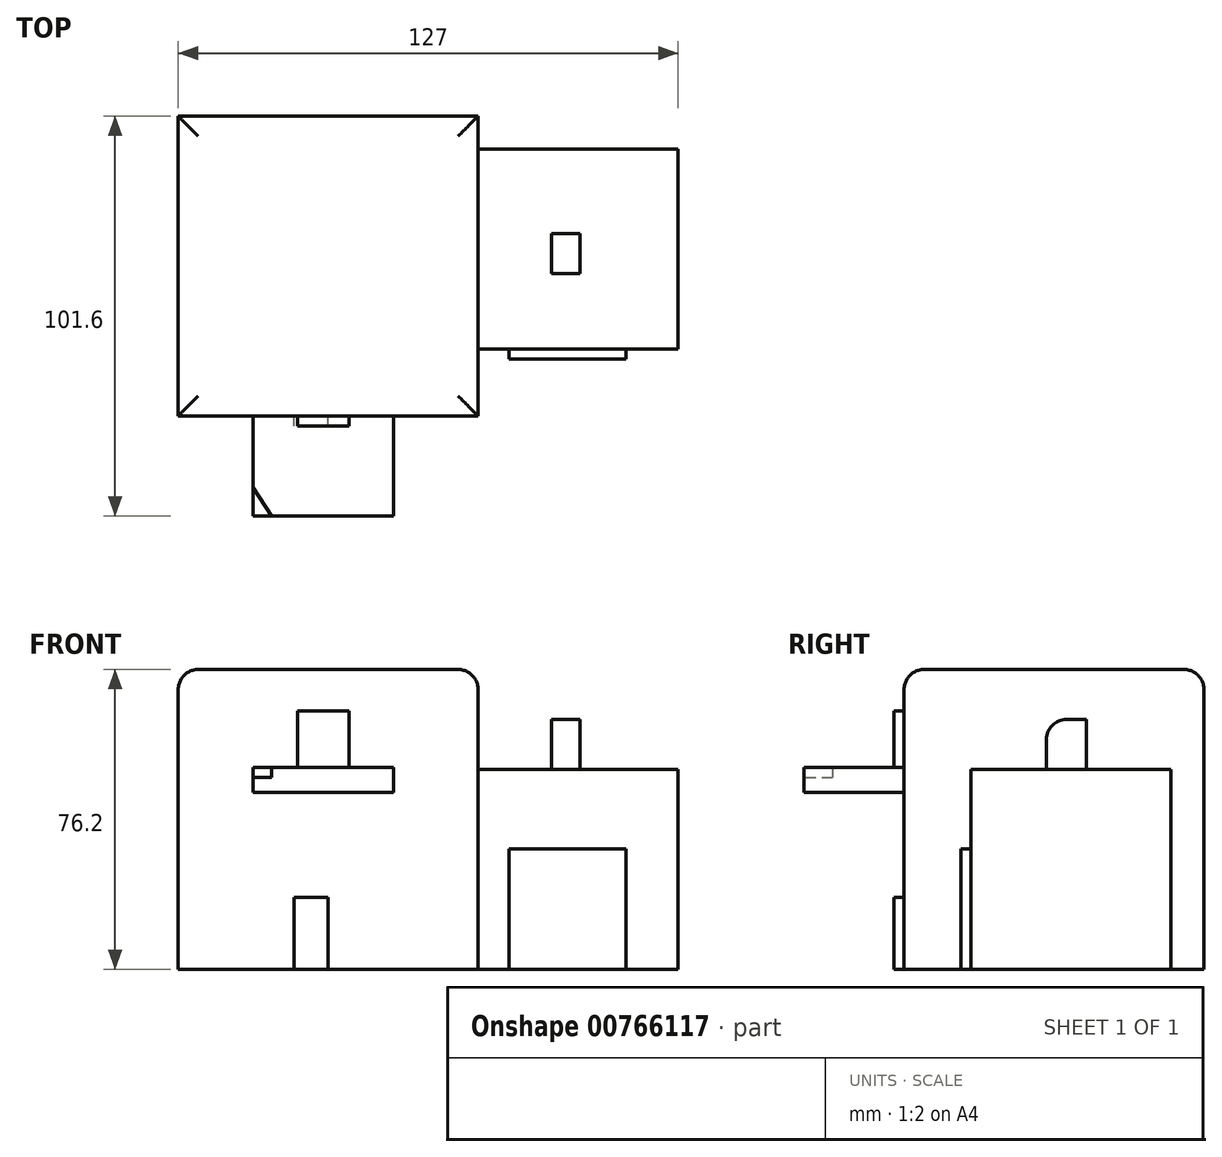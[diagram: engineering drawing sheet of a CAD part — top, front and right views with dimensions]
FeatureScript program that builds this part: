
annotation { "Feature Type Name" : "Feature", "Feature Type Description" : "" }
export const myFeature = defineFeature(function(context is Context, id is Id, definition is map)
    precondition{}
    {
        {
            var Q0;
            Q0=qCreatedBy(makeId("Top.planeOp"),FACE);
            var sketch = newSketch(context, id + "F0", { "sketchPlane" : qUnion([Q0])});
            skLineSegment(sketch, "E0.bottom", {"start": v(0, 0) * mm, "end": v(-76.2, 0) * mm});
            skLineSegment(sketch, "E0.top", {"start": v(0, 76.2) * mm, "end": v(-76.2, 76.2) * mm});
            skLineSegment(sketch, "E0.left", {"start": v(0, 0) * mm, "end": v(0, 76.2) * mm});
            skLineSegment(sketch, "E0.right", {"start": v(-76.2, 0) * mm, "end": v(-76.2, 76.2) * mm});
            skSolve(sketch);
        }
        {
            var Q0;
            Q0=makeQuery(id+"F0.imprint","IMPRINT",FACE,{"disambiguationData":[TD([[makeQuery(id+"F0.imprint","IMPRINT",EDGE,{"derivedFrom":sQuery(id+"F0.wireOp",EDGE,"E0.bottom")}),-1.0]])]});
            extrude(context, id + "F1", {"entities" : qUnion([Q0]), "depth" : 76.2 * mm, "offsetDistance" : 25.4 * mm});
        }
        {
            var Q0;
            Q0=makeQuery(id+"F1.opExtrude","SWEPT_FACE",FACE,{"disambiguationData":[OSD([sQuery(id+"F0.wireOp",EDGE,"E0.left")])]});
            var sketch = newSketch(context, id + "F2", { "sketchPlane" : qUnion([Q0])});
            skLineSegment(sketch, "E1.bottom", {"start": v(17, 0) * mm, "end": v(67.8, 0) * mm});
            skLineSegment(sketch, "E1.top", {"start": v(17, 50.8) * mm, "end": v(67.8, 50.8) * mm});
            skLineSegment(sketch, "E1.left", {"start": v(17, 0) * mm, "end": v(17, 50.8) * mm});
            skLineSegment(sketch, "E1.right", {"start": v(67.8, 0) * mm, "end": v(67.8, 50.8) * mm});
            skSolve(sketch);
        }
        {
            var Q0;
            Q0=makeQuery(id+"F2.imprint","IMPRINT",FACE,{"disambiguationData":[TD([[makeQuery(id+"F2.imprint","IMPRINT",EDGE,{"derivedFrom":sQuery(id+"F2.wireOp",EDGE,"E1.bottom")}),1.0]])]});
            extrude(context, id + "F3", {"entities" : qUnion([Q0]), "operationType" : NewBodyOperationType.ADD, "depth" : 50.8 * mm, "offsetDistance" : 25.4 * mm});
        }
        {
            var Q0;
            Q0=makeQuery(id+"F3.opExtrude","SWEPT_FACE",FACE,{"disambiguationData":[OSD([sQuery(id+"F2.wireOp",EDGE,"E1.top")])]});
            var sketch = newSketch(context, id + "F4", { "sketchPlane" : qUnion([Q0])});
            skLineSegment(sketch, "E2.bottom", {"start": v(25.93, 36.2) * mm, "end": v(18.68, 36.2) * mm});
            skLineSegment(sketch, "E2.top", {"start": v(25.93, 46.31) * mm, "end": v(18.68, 46.31) * mm});
            skLineSegment(sketch, "E2.left", {"start": v(25.93, 36.2) * mm, "end": v(25.93, 46.31) * mm});
            skLineSegment(sketch, "E2.right", {"start": v(18.68, 36.2) * mm, "end": v(18.68, 46.31) * mm});
            skSolve(sketch);
        }
        {
            var Q0;
            Q0=makeQuery(id+"F4.imprint","IMPRINT",FACE,{"disambiguationData":[TD([[makeQuery(id+"F4.imprint","IMPRINT",EDGE,{"derivedFrom":sQuery(id+"F4.wireOp",EDGE,"E2.bottom")}),-1.0]])]});
            extrude(context, id + "F5", {"entities" : qUnion([Q0]), "operationType" : NewBodyOperationType.ADD, "depth" : 12.7 * mm, "offsetDistance" : 25.4 * mm});
        }
        {
            var Q0;
            Q0=makeQuery(id+"F5.opExtrude","CAP_EDGE",EDGE,{"disambiguationData":[OSD([sQuery(id+"F4.wireOp",EDGE,"E2.bottom")])],"isStart":false});
            fillet(context, id + "F6", {"entities" : qUnion([Q0]), "radius" : 5.08 * mm, "tangentPropagation" : true, "allowEdgeOverflow" : false});
        }
        {
            var Q0;
            Q0=makeQuery(id+"F1.opExtrude","SWEPT_FACE",FACE,{"disambiguationData":[OSD([sQuery(id+"F0.wireOp",EDGE,"E0.bottom")])]});
            var sketch = newSketch(context, id + "F7", { "sketchPlane" : qUnion([Q0])});
            skLineSegment(sketch, "E3.bottom", {"start": v(-46.73, 0) * mm, "end": v(-38.14, 0) * mm});
            skLineSegment(sketch, "E3.top", {"start": v(-46.73, 18.26) * mm, "end": v(-38.14, 18.26) * mm});
            skLineSegment(sketch, "E3.left", {"start": v(-46.73, 0) * mm, "end": v(-46.73, 18.26) * mm});
            skLineSegment(sketch, "E3.right", {"start": v(-38.14, 0) * mm, "end": v(-38.14, 18.26) * mm});
            skSolve(sketch);
        }
        {
            var Q0;
            Q0=makeQuery(id+"F7.imprint","IMPRINT",FACE,{"disambiguationData":[TD([[makeQuery(id+"F7.imprint","IMPRINT",EDGE,{"derivedFrom":sQuery(id+"F7.wireOp",EDGE,"E3.bottom")}),-1.0]])]});
            extrude(context, id + "F8", {"entities" : qUnion([Q0]), "operationType" : NewBodyOperationType.ADD, "depth" : 2.54 * mm, "offsetDistance" : 25.4 * mm});
        }
        {
            var Q0;
            Q0=makeQuery(id+"F1.opExtrude","CAP_FACE",FACE,{"disambiguationData":[OSD([sQuery(id+"F0.wireOp",EDGE,"E0.bottom"),sQuery(id+"F0.wireOp",EDGE,"E0.top"),sQuery(id+"F0.wireOp",EDGE,"E0.left"),sQuery(id+"F0.wireOp",EDGE,"E0.right")])],"isStart":false});
            var sketch = newSketch(context, id + "F9", { "sketchPlane" : qUnion([Q0])});
            skSolve(sketch);
        }
        {
            var Q0;
            Q0=makeQuery(id+"F3.opExtrude","SWEPT_FACE",FACE,{"disambiguationData":[OSD([sQuery(id+"F2.wireOp",EDGE,"E1.left")])]});
            var sketch = newSketch(context, id + "F10", { "sketchPlane" : qUnion([Q0])});
            skLineSegment(sketch, "E4.bottom", {"start": v(7.83, 0) * mm, "end": v(37.58, 0) * mm});
            skLineSegment(sketch, "E4.top", {"start": v(7.83, 30.67) * mm, "end": v(37.58, 30.67) * mm});
            skLineSegment(sketch, "E4.left", {"start": v(7.83, 0) * mm, "end": v(7.83, 30.67) * mm});
            skLineSegment(sketch, "E4.right", {"start": v(37.58, 0) * mm, "end": v(37.58, 30.67) * mm});
            skSolve(sketch);
        }
        {
            var Q0;
            Q0=makeQuery(id+"F10.imprint","IMPRINT",FACE,{"disambiguationData":[TD([[makeQuery(id+"F10.imprint","IMPRINT",EDGE,{"derivedFrom":sQuery(id+"F10.wireOp",EDGE,"E4.bottom")}),-1.0]])]});
            extrude(context, id + "F11", {"entities" : qUnion([Q0]), "operationType" : NewBodyOperationType.ADD, "depth" : 2.54 * mm, "offsetDistance" : 25.4 * mm});
        }
        {
            var Q0;
            Q0=makeQuery(id+"F1.opExtrude","CAP_EDGE",EDGE,{"disambiguationData":[OSD([sQuery(id+"F0.wireOp",EDGE,"E0.bottom")])],"isStart":false});
            var Q1;
            Q1=makeQuery(id+"F1.opExtrude","CAP_EDGE",EDGE,{"disambiguationData":[OSD([sQuery(id+"F0.wireOp",EDGE,"E0.left")])],"isStart":false});
            var Q2;
            Q2=makeQuery(id+"F1.opExtrude","CAP_EDGE",EDGE,{"disambiguationData":[OSD([sQuery(id+"F0.wireOp",EDGE,"E0.top")])],"isStart":false});
            var Q3;
            Q3=makeQuery(id+"F1.opExtrude","CAP_EDGE",EDGE,{"disambiguationData":[OSD([sQuery(id+"F0.wireOp",EDGE,"E0.right")])],"isStart":false});
            fillet(context, id + "F12", {"entities" : qUnion([Q0, Q1, Q2, Q3]), "radius" : 5.08 * mm, "tangentPropagation" : true, "allowEdgeOverflow" : false});
        }
        {
            var Q0;
            Q0=makeQuery(id+"F1.opExtrude","SWEPT_FACE",FACE,{"disambiguationData":[OSD([sQuery(id+"F0.wireOp",EDGE,"E0.bottom")])]});
            var sketch = newSketch(context, id + "F13", { "sketchPlane" : qUnion([Q0])});
            skLineSegment(sketch, "E5.bottom", {"start": v(-57.15, 44.98) * mm, "end": v(-21.45, 44.98) * mm});
            skLineSegment(sketch, "E5.top", {"start": v(-57.15, 48.76) * mm, "end": v(-21.45, 48.76) * mm});
            skLineSegment(sketch, "E5.left", {"start": v(-57.15, 44.98) * mm, "end": v(-57.15, 48.76) * mm});
            skLineSegment(sketch, "E5.right", {"start": v(-21.45, 44.98) * mm, "end": v(-21.45, 48.76) * mm});
            skSolve(sketch);
        }
        {
            var Q0;
            Q0=makeQuery(id+"F13.imprint","IMPRINT",FACE,{"disambiguationData":[TD([[makeQuery(id+"F13.imprint","IMPRINT",EDGE,{"derivedFrom":sQuery(id+"F13.wireOp",EDGE,"E5.bottom")}),1.0]])]});
            extrude(context, id + "F14", {"entities" : qUnion([Q0]), "operationType" : NewBodyOperationType.ADD, "depth" : 25.4 * mm, "offsetDistance" : 25.4 * mm});
        }
        {
            var Q0;
            Q0=makeQuery(id+"F14.opExtrude","SWEPT_FACE",FACE,{"disambiguationData":[OSD([sQuery(id+"F13.wireOp",EDGE,"E5.top")])]});
            var sketch = newSketch(context, id + "F15", { "sketchPlane" : qUnion([Q0])});
            skLineSegment(sketch, "E6", {"start": v(-52.47, -25.4) * mm, "end": v(-64.33, -7.2) * mm});
            skLineSegment(sketch, "E7", {"start": v(-48.16, -25.4) * mm, "end": v(-60.44, -6.08) * mm});
            skLineSegment(sketch, "E8", {"start": v(-44.17, -25.4) * mm, "end": v(-60.44, 0) * mm});
            skLineSegment(sketch, "E9", {"start": v(-37.56, -25.4) * mm, "end": v(-55.36, 0) * mm});
            skLineSegment(sketch, "E10", {"start": v(-32.08, -25.4) * mm, "end": v(-50.34, 0) * mm});
            skLineSegment(sketch, "E11", {"start": v(-26.82, -25.4) * mm, "end": v(-47.89, 4.57) * mm});
            skLineSegment(sketch, "E12", {"start": v(-21.45, -25.4) * mm, "end": v(-39.3, 0) * mm});
            skLineSegment(sketch, "E13", {"start": v(-21.45, -12.7) * mm, "end": v(-32.19, 0) * mm});
            skLineSegment(sketch, "E14", {"start": v(-21.45, -6.08) * mm, "end": v(-26.82, 0) * mm});
            skPoint(sketch, "E14.endSnap0", {"position": v(-26.82, -6.35) * mm});
            skSolve(sketch);
        }
        {
            var Q0;
            Q0=makeQuery(id+"F1.opExtrude","SWEPT_FACE",FACE,{"disambiguationData":[OSD([sQuery(id+"F0.wireOp",EDGE,"E0.bottom")])]});
            var sketch = newSketch(context, id + "F16", { "sketchPlane" : qUnion([Q0])});
            skLineSegment(sketch, "E15.bottom", {"start": v(-45.82, 48.76) * mm, "end": v(-32.78, 48.76) * mm});
            skLineSegment(sketch, "E15.top", {"start": v(-45.82, 65.6) * mm, "end": v(-32.78, 65.6) * mm});
            skLineSegment(sketch, "E15.left", {"start": v(-45.82, 48.76) * mm, "end": v(-45.82, 65.6) * mm});
            skLineSegment(sketch, "E15.right", {"start": v(-32.78, 48.76) * mm, "end": v(-32.78, 65.6) * mm});
            skSolve(sketch);
        }
        {
            var Q0;
            Q0=makeQuery(id+"F16.imprint","IMPRINT",FACE,{"disambiguationData":[TD([[makeQuery(id+"F16.imprint","IMPRINT",EDGE,{"derivedFrom":sQuery(id+"F16.wireOp",EDGE,"E15.bottom")}),1.0]])]});
            extrude(context, id + "F17", {"entities" : qUnion([Q0]), "operationType" : NewBodyOperationType.ADD, "depth" : 2.54 * mm, "offsetDistance" : 25.4 * mm});
        }
        {
            var Q0;
            {var subQ0=sQuery(id+"F15.wireOp",EDGE,"E6");var subQ1=sQuery(id+"F13.wireOp",EDGE,"E5.top");var subQ2=makeQuery(id+"F14.opExtrude","CAP_EDGE",EDGE,{"disambiguationData":[OSD([subQ1])],"isStart":false});var subQ3=makeQuery(id+"F15.imprint","INTERSECT",VERTEX,{"derivedFrom":[subQ2,subQ0]});Q0=makeQuery(id+"F15.imprint","IMPRINT",FACE,{"disambiguationData":[TD([[makeQuery(id+"F15.imprint","IMPRINT",EDGE,{"disambiguationData":[TD([[subQ3,-1.0]])],"derivedFrom":subQ2}),1.0]])]});}
            extrude(context, id + "F18", {"entities" : qUnion([Q0]), "operationType" : NewBodyOperationType.ADD, "depth" : 2.54 * mm, "offsetDistance" : 25.4 * mm});
        }
        {
            var Q0;
            {var subQ4=sQuery(id+"F13.wireOp",EDGE,"E5.top");Q0=makeQuery(id+"F18.boolean.opBoolean","SPLIT",FACE,{"disambiguationData":[TD([makeQuery(id+"F1.opExtrude","SWEPT_FACE",FACE,{"disambiguationData":[OSD([sQuery(id+"F0.wireOp",EDGE,"E0.bottom")])]})])],"derivedFrom":makeQuery(id+"F14.opExtrude","SWEPT_FACE",FACE,{"disambiguationData":[OSD([subQ4])]})});}
            extrude(context, id + "F19", {"entities" : qUnion([Q0]), "operationType" : NewBodyOperationType.ADD, "depth" : 2.54 * mm, "offsetDistance" : 25.4 * mm});
        }
    });
